# Revit family: GE6 - Curved 4 Fins
name_source: partatom
category: Furniture
units: mm (PartAtom-declared; Revit-internal decimal feet)

## family parameters
Always vertical = Yes
Cut with Voids When Loaded = No
OmniClass Number = 23.40.20.00
OmniClass Title = General Furniture and Specialties
Room Calculation Point = No
Shared = No
Work Plane-Based = No

## types (3) — shared parameters
Assembly Code = E2020200
Base = Gresham - WHITE PLASTIC
Fins = GABRIEL Byron_15101
Manufacturer = Gresham Office Furniture
Model = GE6
Range = SCREENS
URL = www.gof.co.uk

## per-type parameters (varying)
| type | Fin Height | Product Code |
| Curved - 1200 High | 1200 mm  [stored 3.93701 ft] | GE6E1 |
| Curved - 1600 High | 1600 mm  [stored 5.24934 ft] | GE6E2 |
| Curved - 1800 High | 1800 mm  [stored 5.90551 ft] | GE6E3 |

note: [stored X ft] marks values corroborated as IEEE doubles in the binary element streams (Revit-internal decimal feet)

## geometry (parser evidence)
native form markers: Sweep x4
no freeform markers — native parametric forms only
